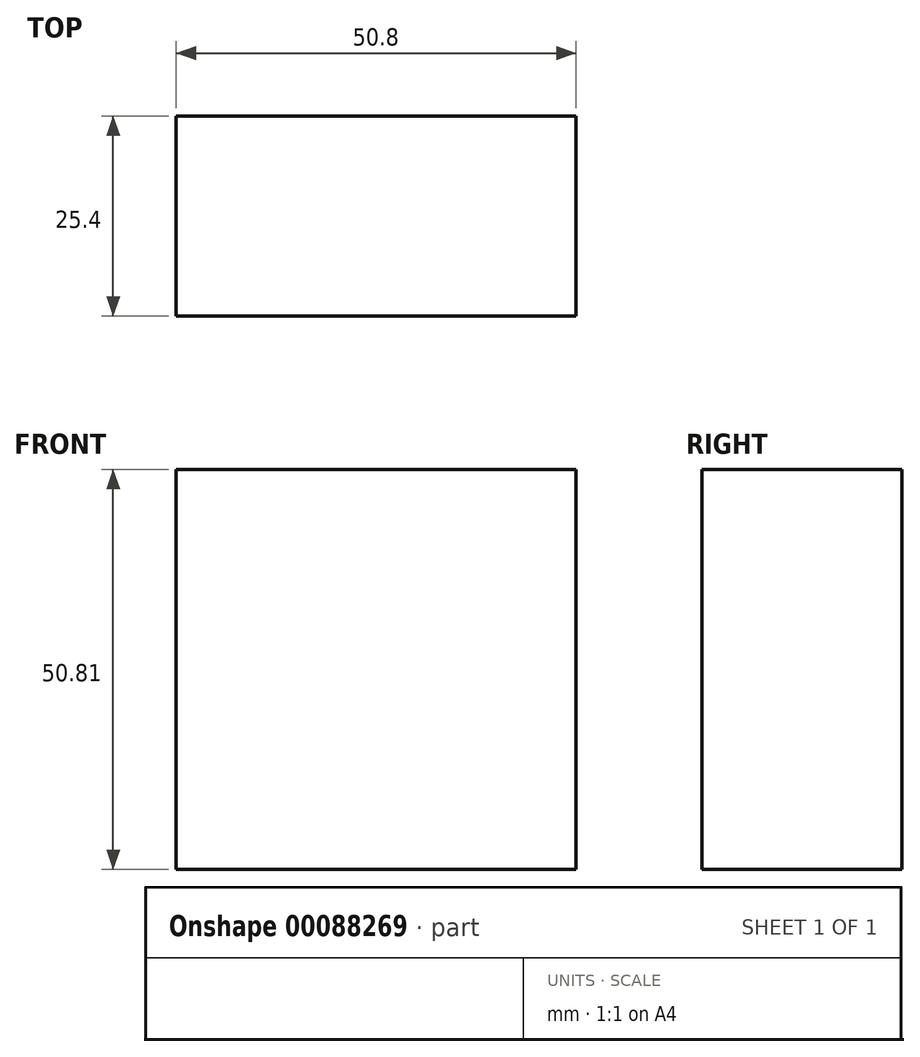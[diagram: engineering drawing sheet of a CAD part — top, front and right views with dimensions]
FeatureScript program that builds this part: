
annotation { "Feature Type Name" : "Feature", "Feature Type Description" : "" }
export const myFeature = defineFeature(function(context is Context, id is Id, definition is map)
    precondition{}
    {
        {
            var Q0;
            Q0=qCreatedBy(makeId("Front.planeOp"),FACE);
            var sketch = newSketch(context, id + "F0", { "sketchPlane" : qUnion([Q0])});
            skLineSegment(sketch, "E0.bottom", {"start": v(-63.5, 9.52) * mm, "end": v(63.5, 9.52) * mm});
            skLineSegment(sketch, "E0.top", {"start": v(-63.5, -9.52) * mm, "end": v(63.5, -9.52) * mm});
            skLineSegment(sketch, "E0.left", {"start": v(-63.5, 9.52) * mm, "end": v(-63.5, -9.52) * mm});
            skLineSegment(sketch, "E0.right", {"start": v(63.5, 9.52) * mm, "end": v(63.5, -9.52) * mm});
            skPoint(sketch, "E0.middle", {"position": v(0, 0) * mm});
            skLineSegment(sketch, "E1", {"start": v(49.97, 39.36) * mm, "end": v(49.97, 0) * mm});
            skArc(sketch, "E2", {"start": v(49.97, 39.36) * mm, "mid": v(55.26, 51) * mm, "end": v(67.52, 54.66) * mm});
            skArc(sketch, "E3.0", {"start": v(29.65, 39.36) * mm, "mid": v(41.91, 66.32) * mm, "end": v(70.29, 74.79) * mm});
            skLineSegment(sketch, "E3.1", {"start": v(29.65, 39.36) * mm, "end": v(29.65, 0) * mm});
            skLineSegment(sketch, "E4", {"start": v(70.29, 74.79) * mm, "end": v(103.92, 74.79) * mm});
            skLineSegment(sketch, "E5", {"start": v(67.52, 54.66) * mm, "end": v(104.37, 54.66) * mm});
            skLineSegment(sketch, "E6.bottom", {"start": v(99.42, 92.08) * mm, "end": v(150.22, 92.08) * mm});
            skLineSegment(sketch, "E6.top", {"start": v(99.42, 41.27) * mm, "end": v(150.22, 41.27) * mm});
            skLineSegment(sketch, "E6.left", {"start": v(99.42, 92.08) * mm, "end": v(99.42, 41.27) * mm});
            skLineSegment(sketch, "E6.right", {"start": v(150.22, 92.08) * mm, "end": v(150.22, 41.27) * mm});
            skPoint(sketch, "E6.middle", {"position": v(124.82, 66.68) * mm});
            skLineSegment(sketch, "E7", {"start": v(99.42, 92.08) * mm, "end": v(-63.5, 9.52) * mm});
            skSolve(sketch);
        }
        {
            var Q0;
            {var subQ3=sQuery(id+"F0.wireOp",EDGE,"E6.bottom");Q0=makeQuery(id+"F0.imprint","IMPRINT",FACE,{"disambiguationData":[TD([[makeQuery(id+"F0.imprint","IMPRINT",EDGE,{"derivedFrom":subQ3}),-1.0]])]});}
            extrude(context, id + "F1", {"entities" : qUnion([Q0]), "depth" : 25.4 * mm});
        }
    });
